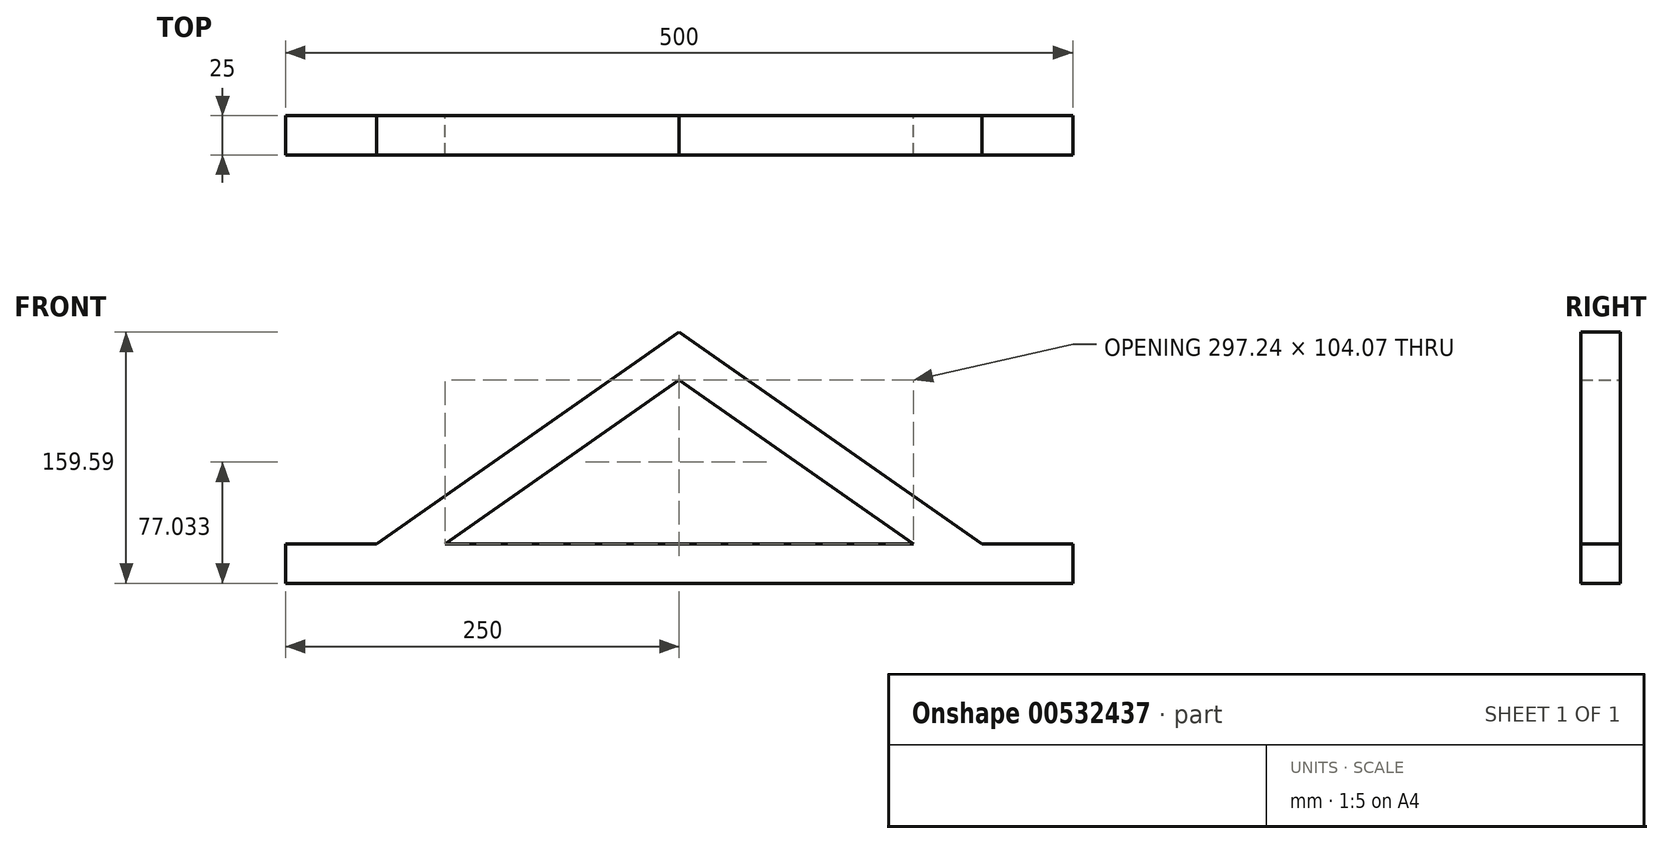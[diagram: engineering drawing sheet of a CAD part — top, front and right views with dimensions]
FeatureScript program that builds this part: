
annotation { "Feature Type Name" : "Feature", "Feature Type Description" : "" }
export const myFeature = defineFeature(function(context is Context, id is Id, definition is map)
    precondition{}
    {
        {
            var Q0;
            Q0=qCreatedBy(makeId("Front.planeOp"),FACE);
            var sketch = newSketch(context, id + "F0", { "sketchPlane" : qUnion([Q0])});
            skLineSegment(sketch, "E0.bottom", {"start": v(-250, 0) * mm, "end": v(250, 0) * mm});
            skLineSegment(sketch, "E0.top", {"start": v(-250, 25) * mm, "end": v(250, 25) * mm});
            skLineSegment(sketch, "E0.left", {"start": v(-250, 0) * mm, "end": v(-250, 25) * mm});
            skLineSegment(sketch, "E0.right", {"start": v(250, 0) * mm, "end": v(250, 25) * mm});
            skPoint(sketch, "E1", {"position": v(0, 0) * mm});
            skLineSegment(sketch, "E2", {"start": v(-192.2, 25) * mm, "end": v(0, 159.59) * mm});
            skLineSegment(sketch, "E3", {"start": v(0, 159.59) * mm, "end": v(0, 159.59) * mm});
            skPoint(sketch, "E3.endSnap0", {"position": v(0, 25) * mm});
            skLineSegment(sketch, "E4", {"start": v(0, 129.07) * mm, "end": v(-148.62, 25) * mm});
            skLineSegment(sketch, "E5.MirrorCS", {"start": v(192.2, 25) * mm, "end": v(0, 159.59) * mm});
            skLineSegment(sketch, "E6.MirrorCS", {"start": v(0, 129.07) * mm, "end": v(148.62, 25) * mm});
            skSolve(sketch);
        }
        {
            var Q0;
            {var subQ0=sQuery(id+"F0.wireOp",EDGE,"E2");Q0=makeQuery(id+"F0.imprint","IMPRINT",FACE,{"disambiguationData":[TD([[makeQuery(id+"F0.imprint","IMPRINT",EDGE,{"derivedFrom":subQ0}),-1.0]])]});}
            var Q1;
            Q1=makeQuery(id+"F0.imprint","IMPRINT",FACE,{"disambiguationData":[TD([[makeQuery(id+"F0.imprint","IMPRINT",EDGE,{"derivedFrom":sQuery(id+"F0.wireOp",EDGE,"E0.bottom")}),1.0]])]});
            extrude(context, id + "F1", {"entities" : qUnion([Q0, Q1]), "depth" : 25 * mm, "offsetDistance" : 25 * mm});
        }
    });
